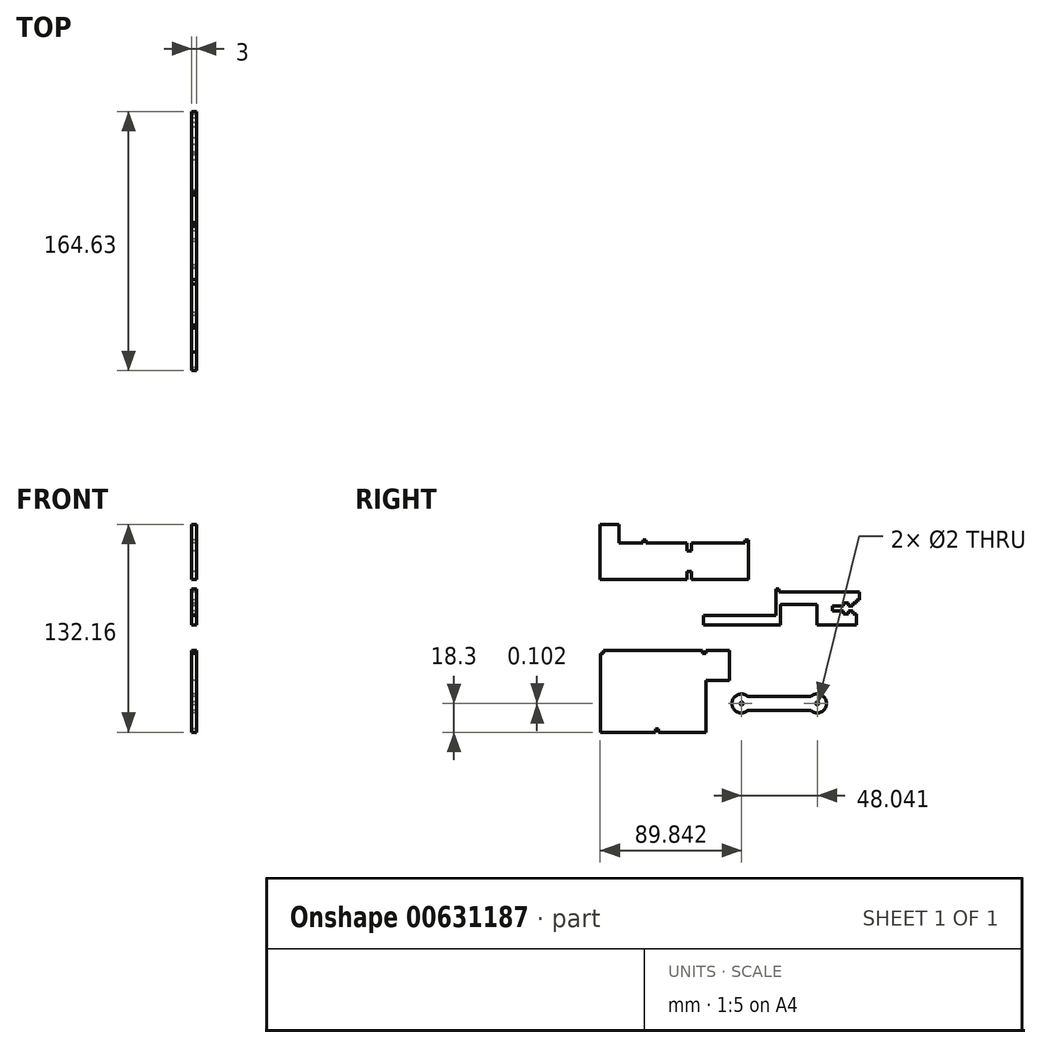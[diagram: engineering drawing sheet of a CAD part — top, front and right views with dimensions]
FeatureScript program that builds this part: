
annotation { "Feature Type Name" : "Feature", "Feature Type Description" : "" }
export const myFeature = defineFeature(function(context is Context, id is Id, definition is map)
    precondition{}
    {
        {
            var Q0;
            Q0=qCreatedBy(makeId("Right.planeOp"),FACE);
            var sketch = newSketch(context, id + "F0", { "sketchPlane" : qUnion([Q0])});
            skLineSegment(sketch, "E0", {"start": v(-65.59, -47.48) * mm, "end": v(-65.59, 2.52) * mm});
            skLineSegment(sketch, "E1", {"start": v(-65.59, 2.52) * mm, "end": v(-63.59, 2.52) * mm});
            skLineSegment(sketch, "E2", {"start": v(-63.59, 2.52) * mm, "end": v(-63.59, 4.52) * mm});
            skLineSegment(sketch, "E3", {"start": v(-0.59, 4.52) * mm, "end": v(-0.59, 2.52) * mm});
            skLineSegment(sketch, "E4", {"start": v(-0.59, 2.52) * mm, "end": v(1.41, 2.52) * mm});
            skLineSegment(sketch, "E5", {"start": v(1.41, 2.52) * mm, "end": v(1.41, 4.52) * mm});
            skLineSegment(sketch, "E6", {"start": v(-63.59, 4.52) * mm, "end": v(-0.59, 4.52) * mm});
            skLineSegment(sketch, "E7", {"start": v(1.41, 4.52) * mm, "end": v(16.41, 4.52) * mm});
            skLineSegment(sketch, "E8", {"start": v(16.41, 4.52) * mm, "end": v(16.41, -14.48) * mm});
            skLineSegment(sketch, "E9", {"start": v(16.41, -14.48) * mm, "end": v(1.41, -14.48) * mm});
            skLineSegment(sketch, "E10", {"start": v(1.41, -14.48) * mm, "end": v(1.41, -47.48) * mm});
            skLineSegment(sketch, "E11", {"start": v(1.41, -47.48) * mm, "end": v(-28.59, -47.48) * mm});
            skLineSegment(sketch, "E12", {"start": v(-28.59, -47.48) * mm, "end": v(-28.59, -45.48) * mm});
            skLineSegment(sketch, "E13", {"start": v(-28.59, -45.48) * mm, "end": v(-30.59, -45.48) * mm});
            skLineSegment(sketch, "E14", {"start": v(-30.59, -45.48) * mm, "end": v(-30.59, -47.48) * mm});
            skLineSegment(sketch, "E15", {"start": v(-30.59, -47.48) * mm, "end": v(-65.59, -47.48) * mm});
            skSolve(sketch);
        }
        {
            var Q0;
            Q0=makeQuery(id+"F0.imprint","IMPRINT",FACE,{"disambiguationData":[TD([[makeQuery(id+"F0.imprint","IMPRINT",EDGE,{"derivedFrom":sQuery(id+"F0.wireOp",EDGE,"E0")}),-1.0]])]});
            extrude(context, id + "F1", {"entities" : qUnion([Q0]), "depth" : 3 * mm, "offsetDistance" : 25 * mm});
        }
        {
            var Q0;
            Q0=qCreatedBy(makeId("Right.planeOp"),FACE);
            var sketch = newSketch(context, id + "F2", { "sketchPlane" : qUnion([Q0])});
            skLineSegment(sketch, "E16", {"start": v(-65.63, 49.68) * mm, "end": v(-65.63, 84.68) * mm});
            skLineSegment(sketch, "E17", {"start": v(-65.63, 84.68) * mm, "end": v(-53.63, 84.68) * mm});
            skLineSegment(sketch, "E18", {"start": v(-53.63, 84.68) * mm, "end": v(-53.63, 72.68) * mm});
            skLineSegment(sketch, "E19", {"start": v(-53.63, 72.68) * mm, "end": v(-38.63, 72.68) * mm});
            skLineSegment(sketch, "E20", {"start": v(-38.63, 72.68) * mm, "end": v(-38.63, 74.68) * mm});
            skLineSegment(sketch, "E21", {"start": v(-38.63, 74.68) * mm, "end": v(-36.63, 74.68) * mm});
            skLineSegment(sketch, "E22", {"start": v(-36.63, 74.68) * mm, "end": v(-36.63, 72.68) * mm});
            skLineSegment(sketch, "E23", {"start": v(-36.63, 72.68) * mm, "end": v(-10.63, 72.68) * mm});
            skLineSegment(sketch, "E24", {"start": v(-10.63, 72.68) * mm, "end": v(-10.63, 67.68) * mm});
            skLineSegment(sketch, "E25", {"start": v(-10.63, 67.68) * mm, "end": v(-7.63, 67.68) * mm});
            skLineSegment(sketch, "E26", {"start": v(-7.63, 67.68) * mm, "end": v(-7.63, 72.68) * mm});
            skLineSegment(sketch, "E27", {"start": v(-7.63, 72.68) * mm, "end": v(26.37, 72.68) * mm});
            skLineSegment(sketch, "E28", {"start": v(26.37, 72.68) * mm, "end": v(26.37, 74.68) * mm});
            skLineSegment(sketch, "E29", {"start": v(26.37, 74.68) * mm, "end": v(28.37, 74.68) * mm});
            skLineSegment(sketch, "E30", {"start": v(28.37, 74.68) * mm, "end": v(28.37, 49.68) * mm});
            skLineSegment(sketch, "E31", {"start": v(28.37, 49.68) * mm, "end": v(-7.63, 49.68) * mm});
            skLineSegment(sketch, "E32", {"start": v(-7.63, 49.68) * mm, "end": v(-7.63, 54.68) * mm});
            skLineSegment(sketch, "E33", {"start": v(-7.63, 54.68) * mm, "end": v(-10.63, 54.68) * mm});
            skLineSegment(sketch, "E34", {"start": v(-10.63, 54.68) * mm, "end": v(-10.63, 49.68) * mm});
            skLineSegment(sketch, "E35", {"start": v(-10.63, 49.68) * mm, "end": v(-65.63, 49.68) * mm});
            skSolve(sketch);
        }
        {
            var Q0;
            Q0=makeQuery(id+"F2.imprint","IMPRINT",FACE,{"disambiguationData":[TD([[makeQuery(id+"F2.imprint","IMPRINT",EDGE,{"derivedFrom":sQuery(id+"F2.wireOp",EDGE,"E16")}),-1.0]])]});
            extrude(context, id + "F3", {"entities" : qUnion([Q0]), "depth" : 3 * mm, "offsetDistance" : 25 * mm});
        }
        {
            var Q0;
            Q0=qCreatedBy(makeId("Right.planeOp"),FACE);
            var sketch = newSketch(context, id + "F4", { "sketchPlane" : qUnion([Q0])});
            skLineSegment(sketch, "E36", {"start": v(0, 26.67) * mm, "end": v(0, 20.67) * mm});
            skLineSegment(sketch, "E37", {"start": v(0, 20.67) * mm, "end": v(49, 20.67) * mm});
            skLineSegment(sketch, "E38", {"start": v(49, 20.67) * mm, "end": v(49, 33.67) * mm});
            skLineSegment(sketch, "E39", {"start": v(49, 33.67) * mm, "end": v(72, 33.67) * mm});
            skLineSegment(sketch, "E40", {"start": v(72, 33.67) * mm, "end": v(72, 20.67) * mm});
            skLineSegment(sketch, "E41", {"start": v(72, 20.67) * mm, "end": v(97, 20.67) * mm});
            skLineSegment(sketch, "E42", {"start": v(97, 20.67) * mm, "end": v(97, 27.67) * mm});
            skLineSegment(sketch, "E43", {"start": v(97, 27.67) * mm, "end": v(95, 27.67) * mm});
            skLineSegment(sketch, "E44", {"start": v(95, 27.67) * mm, "end": v(95, 29.67) * mm});
            skLineSegment(sketch, "E45", {"start": v(82, 29.67) * mm, "end": v(82, 32.67) * mm});
            skLineSegment(sketch, "E46", {"start": v(95, 29.67) * mm, "end": v(92, 29.67) * mm});
            skLineSegment(sketch, "E47", {"start": v(92, 29.67) * mm, "end": v(92, 27.67) * mm});
            skLineSegment(sketch, "E48", {"start": v(92, 27.67) * mm, "end": v(89, 27.67) * mm});
            skLineSegment(sketch, "E49", {"start": v(89, 27.67) * mm, "end": v(89, 29.67) * mm});
            skLineSegment(sketch, "E50", {"start": v(89, 29.67) * mm, "end": v(82, 29.67) * mm});
            skLineSegment(sketch, "E51", {"start": v(82, 32.67) * mm, "end": v(89, 32.67) * mm});
            skLineSegment(sketch, "E52", {"start": v(89, 32.67) * mm, "end": v(89, 34.67) * mm});
            skLineSegment(sketch, "E53", {"start": v(89, 34.67) * mm, "end": v(92, 34.67) * mm});
            skLineSegment(sketch, "E54", {"start": v(92, 34.67) * mm, "end": v(92, 32.67) * mm});
            skLineSegment(sketch, "E55", {"start": v(92, 32.67) * mm, "end": v(95, 32.67) * mm});
            skLineSegment(sketch, "E56", {"start": v(95, 32.67) * mm, "end": v(95, 34.67) * mm});
            skLineSegment(sketch, "E57", {"start": v(95, 34.67) * mm, "end": v(97, 34.67) * mm});
            skLineSegment(sketch, "E58", {"start": v(97, 34.67) * mm, "end": v(97, 36.67) * mm});
            skLineSegment(sketch, "E59", {"start": v(97, 36.67) * mm, "end": v(99, 36.67) * mm});
            skLineSegment(sketch, "E60", {"start": v(99, 36.67) * mm, "end": v(99, 41.67) * mm});
            skLineSegment(sketch, "E61", {"start": v(99, 41.67) * mm, "end": v(48, 41.67) * mm});
            skLineSegment(sketch, "E62", {"start": v(48, 41.67) * mm, "end": v(48, 43.67) * mm});
            skLineSegment(sketch, "E63", {"start": v(48, 43.67) * mm, "end": v(46, 43.67) * mm});
            skLineSegment(sketch, "E64", {"start": v(46, 43.67) * mm, "end": v(46, 26.67) * mm});
            skLineSegment(sketch, "E65", {"start": v(46, 26.67) * mm, "end": v(0, 26.67) * mm});
            skSolve(sketch);
        }
        {
            var Q0;
            Q0=qCreatedBy(makeId("Right.planeOp"),FACE);
            var sketch = newSketch(context, id + "F5", { "sketchPlane" : qUnion([Q0])});
            skCircle(sketch, "E66", {"center": v(24.1, -29.17) * mm, "radius": 6 * mm});
            skCircle(sketch, "E67", {"center": v(72.1, -29.17) * mm, "radius": 6 * mm});
            skLineSegment(sketch, "E68", {"start": v(28.13, -33.62) * mm, "end": v(68.07, -33.62) * mm});
            skLineSegment(sketch, "E69", {"start": v(68.07, -24.73) * mm, "end": v(28.13, -24.73) * mm});
            skCircle(sketch, "E70", {"center": v(24.1, -29.17) * mm, "radius": 1 * mm});
            skCircle(sketch, "E71", {"center": v(72.1, -29.17) * mm, "radius": 1 * mm});
            skSolve(sketch);
        }
        {
            var Q0;
            Q0=makeQuery(id+"F4.imprint","IMPRINT",FACE,{"disambiguationData":[TD([[makeQuery(id+"F4.imprint","IMPRINT",EDGE,{"derivedFrom":sQuery(id+"F4.wireOp",EDGE,"E36")}),1.0]])]});
            extrude(context, id + "F6", {"entities" : qUnion([Q0]), "depth" : 3 * mm, "offsetDistance" : 25 * mm});
        }
        {
            var Q0;
            {var subQ0=sQuery(id+"F5.wireOp",EDGE,"E68");Q0=makeQuery(id+"F5.imprint","IMPRINT",FACE,{"disambiguationData":[TD([[makeQuery(id+"F5.imprint","IMPRINT",EDGE,{"derivedFrom":subQ0}),1.0]])]});}
            var Q1;
            Q1=makeQuery(id+"F5.imprint","IMPRINT",FACE,{"disambiguationData":[TD([[makeQuery(id+"F5.imprint","IMPRINT",EDGE,{"derivedFrom":sQuery(id+"F5.wireOp",EDGE,"E71")}),-1.0]])]});
            var Q2;
            Q2=makeQuery(id+"F5.imprint","IMPRINT",FACE,{"disambiguationData":[TD([[makeQuery(id+"F5.imprint","IMPRINT",EDGE,{"derivedFrom":sQuery(id+"F5.wireOp",EDGE,"E70")}),-1.0]])]});
            var Q3;
            Q3=makeQuery(id+"F5.imprint","IMPRINT",FACE,{"disambiguationData":[TD([[makeQuery(id+"F5.imprint","IMPRINT",EDGE,{"derivedFrom":sQuery(id+"F5.wireOp",EDGE,"E71")}),1.0]])]});
            var Q4;
            Q4=makeQuery(id+"F5.imprint","IMPRINT",FACE,{"disambiguationData":[TD([[makeQuery(id+"F5.imprint","IMPRINT",EDGE,{"derivedFrom":sQuery(id+"F5.wireOp",EDGE,"E70")}),1.0]])]});
            extrude(context, id + "F7", {"entities" : qUnion([Q0, Q1, Q2, Q3, Q4]), "depth" : 3 * mm, "offsetDistance" : 25 * mm});
        }
        {
            var Q0;
            Q0=qCreatedBy(makeId("Right.planeOp"),FACE);
            var sketch = newSketch(context, id + "F8", { "sketchPlane" : qUnion([Q0])});
            skCircle(sketch, "E72", {"center": v(72.36, -29) * mm, "radius": 1.4 * mm});
            skCircle(sketch, "E73", {"center": v(24.21, -29.18) * mm, "radius": 1.48 * mm});
            skSolve(sketch);
        }
        {
            var Q0;
            Q0=sQuery(id+"F8.wireOp",VERTEX,"E73.center");
            var Q1;
            Q1=makeQuery(id+"F7.opExtrude","SWEPT_BODY",BODY,{"disambiguationData":[OSD([sQuery(id+"F5.wireOp",EDGE,"E66"),sQuery(id+"F5.wireOp",EDGE,"E67"),sQuery(id+"F5.wireOp",EDGE,"E68"),sQuery(id+"F5.wireOp",EDGE,"E69")])]});
            hole(context, id + "F9", {"style" : HoleStyle.SIMPLE, "endStyle" : HoleEndStyle.THROUGH, "oppositeDirection" : true, "holeDiameter" : 2 * mm, "majorDiameter" : 5 * mm, "isTappedThrough" : true, "tappedDepth" : 12 * mm, "tapClearance" : 3, "locations" : qUnion([Q0]), "scope" : qUnion([Q1])});
        }
        {
            var Q0;
            Q0=qCreatedBy(makeId("Right.planeOp"),FACE);
            var sketch = newSketch(context, id + "F10", { "sketchPlane" : qUnion([Q0])});
            skCircle(sketch, "E74", {"center": v(72.25, -29.08) * mm, "radius": 1.13 * mm});
            skSolve(sketch);
        }
        {
            var Q0;
            Q0=sQuery(id+"F10.wireOp",VERTEX,"E74.center");
            var Q1;
            Q1=makeQuery(id+"F7.opExtrude","SWEPT_BODY",BODY,{"disambiguationData":[OSD([sQuery(id+"F5.wireOp",EDGE,"E66"),sQuery(id+"F5.wireOp",EDGE,"E67"),sQuery(id+"F5.wireOp",EDGE,"E68"),sQuery(id+"F5.wireOp",EDGE,"E69")])]});
            hole(context, id + "F11", {"style" : HoleStyle.SIMPLE, "endStyle" : HoleEndStyle.THROUGH, "oppositeDirection" : true, "holeDiameter" : 2 * mm, "majorDiameter" : 5 * mm, "isTappedThrough" : true, "tappedDepth" : 12 * mm, "tapClearance" : 3, "locations" : qUnion([Q0]), "scope" : qUnion([Q1])});
        }
    });
